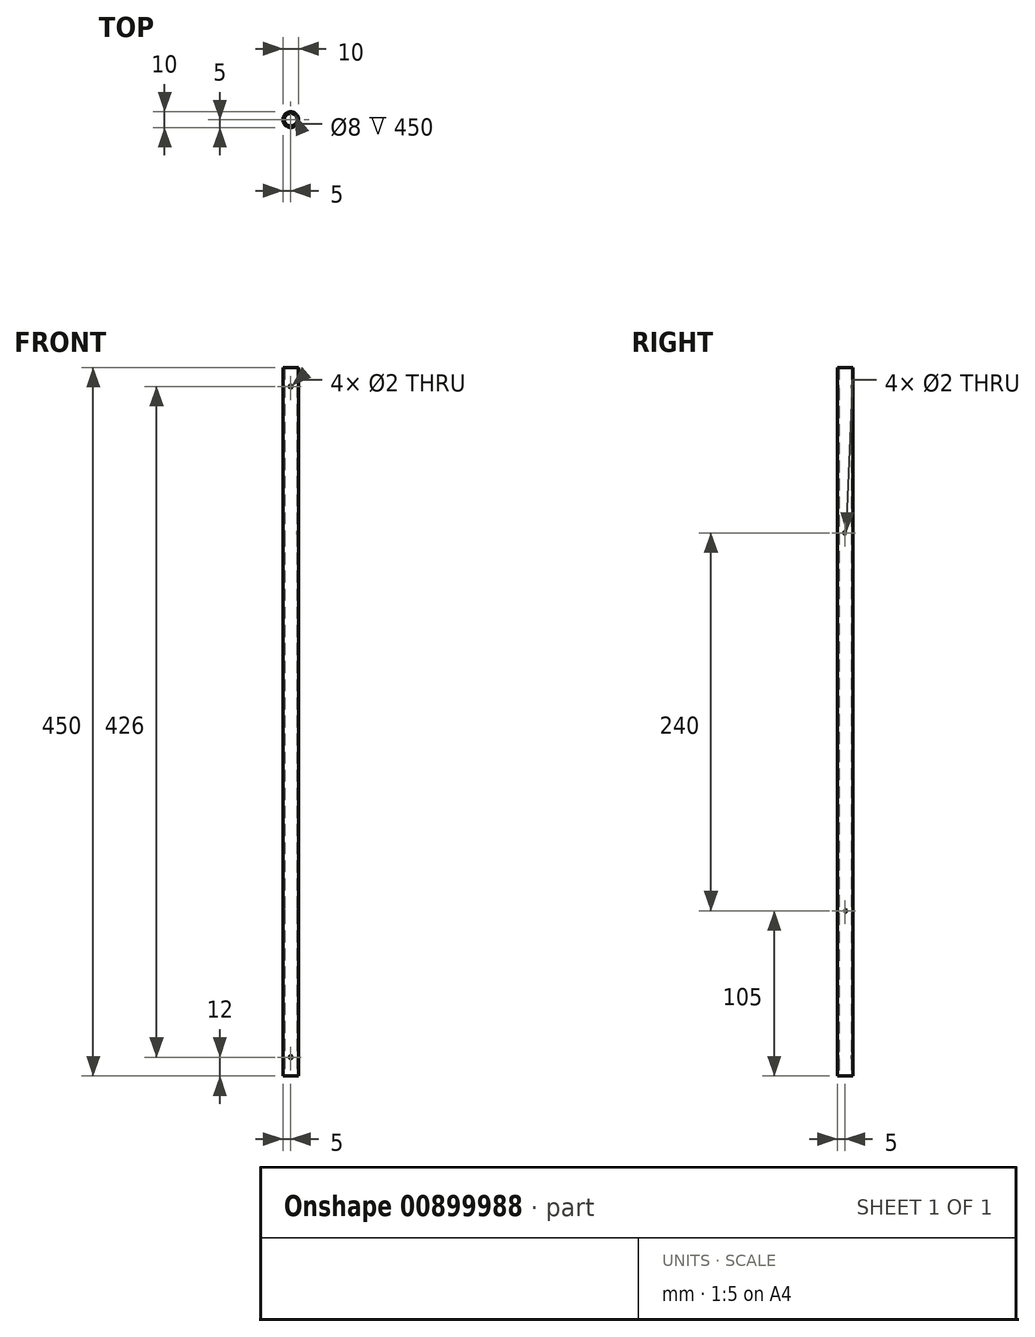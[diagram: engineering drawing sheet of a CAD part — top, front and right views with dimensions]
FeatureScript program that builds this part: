
annotation { "Feature Type Name" : "Feature", "Feature Type Description" : "" }
export const myFeature = defineFeature(function(context is Context, id is Id, definition is map)
    precondition{}
    {
        {
            var Q0;
            Q0=qCreatedBy(makeId("Top.planeOp"),FACE);
            var sketch = newSketch(context, id + "F0", { "sketchPlane" : qUnion([Q0])});
            skCircle(sketch, "E0", {"center": v(0, 0) * mm, "radius": 4 * mm});
            skCircle(sketch, "E1", {"center": v(0, 0) * mm, "radius": 5 * mm});
            skSolve(sketch);
        }
        {
            var Q0;
            Q0=qSketchRegion(id+"F0",true);
            extrude(context, id + "F1", {"entities" : qUnion([Q0]), "endBound" : BoundingType.SYMMETRIC, "depth" : 450 * mm, "offsetDistance" : 25 * mm});
        }
        {
            var Q0;
            Q0=qCreatedBy(makeId("Front.planeOp"),FACE);
            var sketch = newSketch(context, id + "F2", { "sketchPlane" : qUnion([Q0])});
            skCircle(sketch, "E2", {"center": v(0, 213) * mm, "radius": 1 * mm});
            skCircle(sketch, "E3.1.0", {"center": v(0, -213) * mm, "radius": 1 * mm});
            skPoint(sketch, "E3.center", {"position": v(0, 0) * mm});
            skSolve(sketch);
        }
        {
            var Q0;
            Q0 = qSketchRegion(id + "F2", true);
            extrude(context, id + "F3", {"entities" : qUnion([Q0]), "operationType" : NewBodyOperationType.REMOVE, "endBound" : BoundingType.THROUGH_ALL, "oppositeDirection" : true, "depth" : 25 * mm, "offsetDistance" : 25 * mm, "hasSecondDirection" : true, "secondDirectionBound" : SecondDirectionBoundingType.THROUGH_ALL, "secondDirectionOppositeDirection" : false, "secondDirectionDepth" : 25 * mm});
        }
        {
            var Q0;
            Q0=qCreatedBy(makeId("Right.planeOp"),FACE);
            var sketch = newSketch(context, id + "F4", { "sketchPlane" : qUnion([Q0])});
            skCircle(sketch, "E4", {"center": v(0, 120) * mm, "radius": 1 * mm});
            skCircle(sketch, "E5", {"center": v(0, -120) * mm, "radius": 1 * mm});
            skSolve(sketch);
        }
        {
            var Q0;
            Q0 = qSketchRegion(id + "F4", true);
            extrude(context, id + "F5", {"entities" : qUnion([Q0]), "operationType" : NewBodyOperationType.REMOVE, "endBound" : BoundingType.THROUGH_ALL, "oppositeDirection" : true, "depth" : 25 * mm, "offsetDistance" : 25 * mm, "hasSecondDirection" : true, "secondDirectionBound" : SecondDirectionBoundingType.THROUGH_ALL, "secondDirectionOppositeDirection" : false, "secondDirectionDepth" : 25 * mm});
        }
    });
